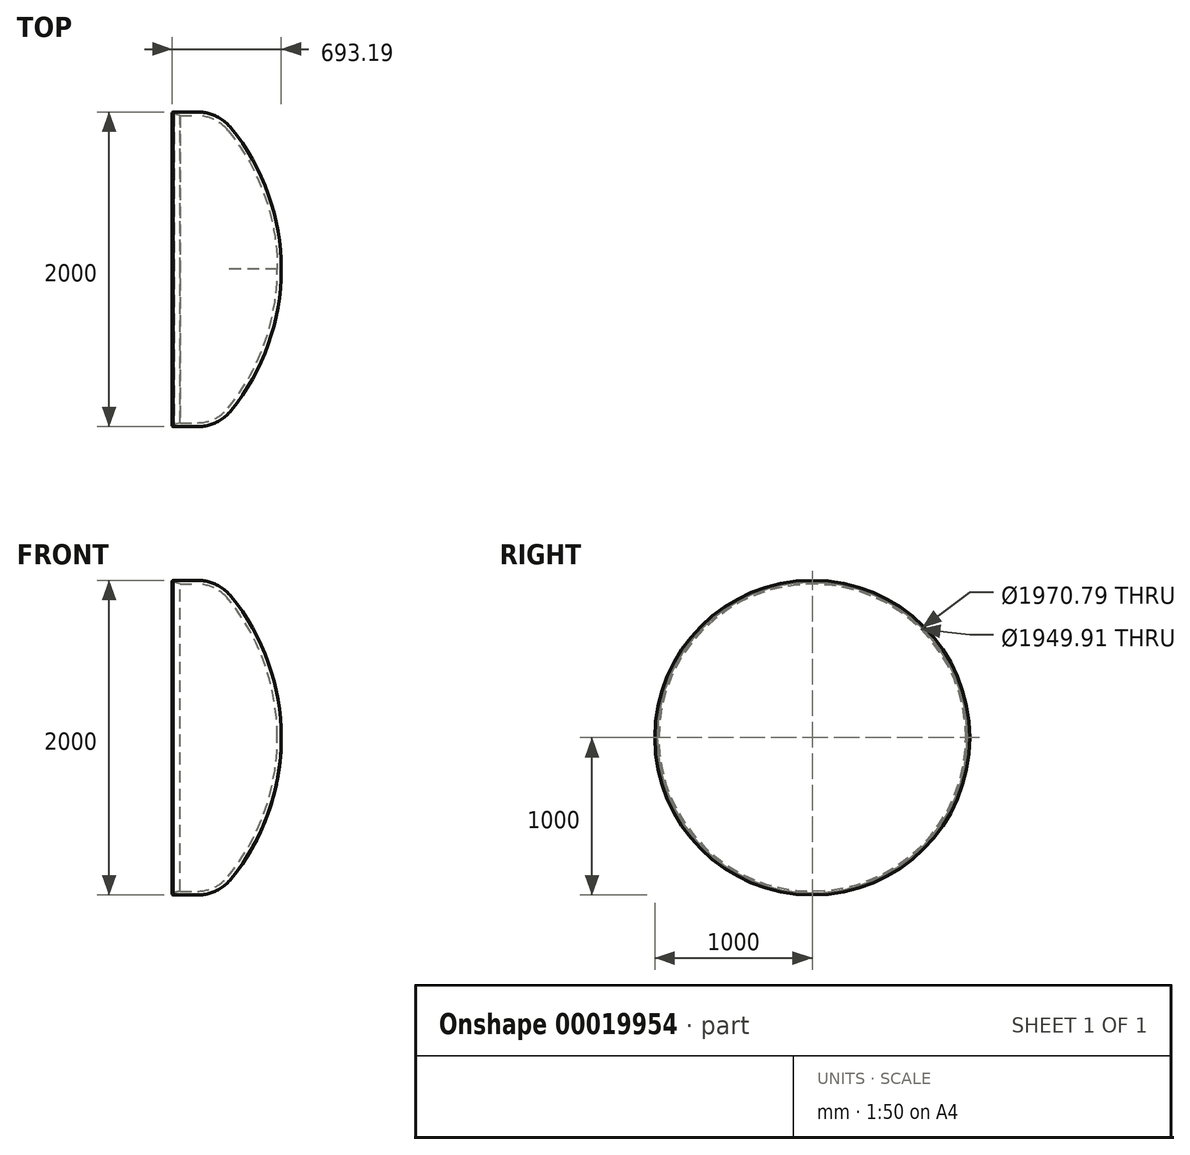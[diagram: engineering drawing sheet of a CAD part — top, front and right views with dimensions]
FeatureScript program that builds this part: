
annotation { "Feature Type Name" : "Feature", "Feature Type Description" : "" }
export const myFeature = defineFeature(function(context is Context, id is Id, definition is map)
    precondition{}
    {
        {
            var Q0;
            Q0=qCreatedBy(makeId("Front.planeOp"),FACE);
            var sketch = newSketch(context, id + "F0", { "sketchPlane" : qUnion([Q0])});
            skLineSegment(sketch, "E0", {"start": v(731.8, 1000) * mm, "end": v(1015.2, 1000) * mm});
            skArc(sketch, "E1.trimOffspring", {"start": v(1400, 0) * mm, "mid": v(1297.4, 526.02) * mm, "end": v(1004.68, 974.95) * mm});
            skArc(sketch, "E2.trimOffspring", {"start": v(1425, 0) * mm, "mid": v(1318.58, 540.36) * mm, "end": v(1015.2, 1000) * mm});
            skLineSegment(sketch, "E3", {"start": v(1425, 0) * mm, "end": v(895, 0) * mm, "construction": true});
            skLineSegment(sketch, "E4", {"start": v(1004.68, 974.95) * mm, "end": v(781.77, 974.95) * mm});
            skLineSegment(sketch, "E5", {"start": v(895, 0) * mm, "end": v(895, 974.95) * mm, "construction": true});
            skLineSegment(sketch, "E6", {"start": v(895, 0) * mm, "end": v(895, -975) * mm, "construction": true});
            skLineSegment(sketch, "E7", {"start": v(731.8, 1000) * mm, "end": v(731.8, 974.95) * mm, "construction": true});
            skPoint(sketch, "E8.trimOffspring.end.orphan", {"position": v(731.8, -1000) * mm});
            skPoint(sketch, "E8.trimOffspring.start.orphan", {"position": v(731.8, -974.95) * mm});
            skLineSegment(sketch, "E9", {"start": v(1400, 0) * mm, "end": v(1425, 0) * mm});
            skLineSegment(sketch, "E10", {"start": v(731.8, 1000) * mm, "end": v(731.8, 985.4) * mm});
            skLineSegment(sketch, "E11", {"start": v(731.8, 985.4) * mm, "end": v(745.58, 985.4) * mm});
            skLineSegment(sketch, "E12", {"start": v(781.77, 974.95) * mm, "end": v(745.58, 985.4) * mm});
            skSolve(sketch);
        }
        {
            var Q0;
            Q0=makeQuery(id+"F0.imprint","IMPRINT",FACE,{"disambiguationData":[TD([[makeQuery(id+"F0.imprint","IMPRINT",EDGE,{"derivedFrom":sQuery(id+"F0.wireOp",EDGE,"E0")}),-1.0]])]});
            var Q1;
            Q1=sQuery(id+"F0.wireOp",EDGE,"E3");
            revolve(context, id + "F1", {"entities" : qUnion([Q0]), "axis" : qUnion([Q1]), "revolveType" : RevolveType.FULL});
        }
        {
            var Q0;
            Q0=makeQuery(id+"F1.opRevolve","SWEPT_EDGE",EDGE,{"disambiguationData":[OSD([sQuery(id+"F0.wireOp",EDGE,"E1.trimOffspring"),sQuery(id+"F0.wireOp",EDGE,"E4")])]});
            fillet(context, id + "F2", {"entities" : qUnion([Q0]), "radius" : 250 * mm, "tangentPropagation" : true, "allowEdgeOverflow" : false});
        }
        {
            var Q0;
            Q0=makeQuery(id+"F1.opRevolve","SWEPT_EDGE",EDGE,{"disambiguationData":[OSD([sQuery(id+"F0.wireOp",EDGE,"E0"),sQuery(id+"F0.wireOp",EDGE,"E2.trimOffspring")])]});
            fillet(context, id + "F3", {"entities" : qUnion([Q0]), "radius" : 275 * mm, "tangentPropagation" : true, "allowEdgeOverflow" : false});
        }
        {
            var Q0;
            Q0=makeQuery(id+"F1.opRevolve","SWEPT_EDGE",EDGE,{"disambiguationData":[OSD([sQuery(id+"F0.wireOp",EDGE,"E0"),sQuery(id+"F0.wireOp",EDGE,"E10")])]});
            var Q1;
            Q1=makeQuery(id+"F1.opRevolve","SWEPT_EDGE",EDGE,{"disambiguationData":[OSD([sQuery(id+"F0.wireOp",EDGE,"E10"),sQuery(id+"F0.wireOp",EDGE,"E11")])]});
            chamfer(context, id + "F4", {"entities" : qUnion([Q0, Q1]), "width" : 5 * mm, "tangentPropagation" : true});
        }
    });
